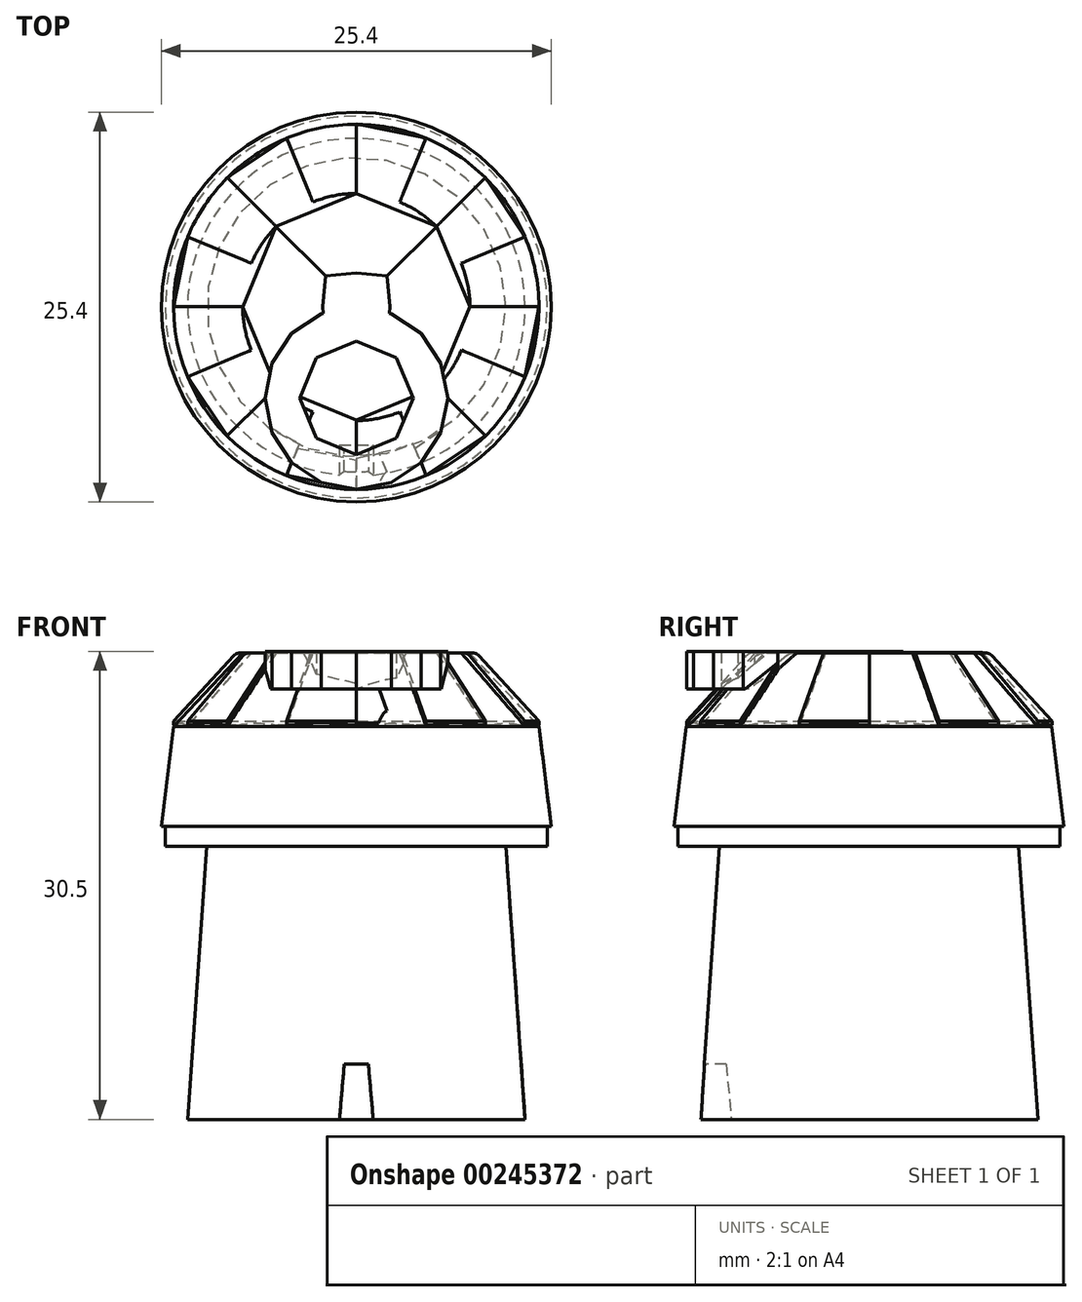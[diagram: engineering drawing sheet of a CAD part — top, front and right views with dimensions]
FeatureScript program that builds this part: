
annotation { "Feature Type Name" : "Feature", "Feature Type Description" : "" }
export const myFeature = defineFeature(function(context is Context, id is Id, definition is map)
    precondition{}
    {
        {
            var Q0;
            Q0=qCreatedBy(makeId("Front.planeOp"),FACE);
            var sketch = newSketch(context, id + "F0", { "sketchPlane" : qUnion([Q0])});
            skLineSegment(sketch, "E0", {"start": v(0, 0) * mm, "end": v(5.5, 0) * mm});
            skLineSegment(sketch, "E1", {"start": v(0, 8.9) * mm, "end": v(4.87, 8.9) * mm});
            skLineSegment(sketch, "E2", {"start": v(4.87, 8.9) * mm, "end": v(5.5, 0) * mm});
            skLineSegment(sketch, "E3", {"start": v(4.87, 8.9) * mm, "end": v(6.22, 8.9) * mm});
            skLineSegment(sketch, "E4", {"start": v(6.22, 8.9) * mm, "end": v(6.22, 9.55) * mm});
            skLineSegment(sketch, "E5", {"start": v(6.22, 9.55) * mm, "end": v(6.35, 9.55) * mm});
            skLineSegment(sketch, "E6", {"start": v(0, 0) * mm, "end": v(0, 15.2) * mm});
            skLineSegment(sketch, "E7", {"start": v(11.32, 12.8) * mm, "end": v(-3.84, 12.8) * mm, "construction": true});
            skLineSegment(sketch, "E8", {"start": v(5.95, 12.8) * mm, "end": v(6.35, 9.55) * mm});
            skLineSegment(sketch, "E9", {"start": v(15.11, 15.2) * mm, "end": v(0, 15.2) * mm, "construction": true});
            skLineSegment(sketch, "E10", {"start": v(0, 15.2) * mm, "end": v(3.7, 15.2) * mm});
            skLineSegment(sketch, "E11", {"start": v(3.7, 15.2) * mm, "end": v(5.95, 12.8) * mm});
            skSolve(sketch);
        }
        {
            var Q0;
            Q0=qSketchRegion(id+"F0",true);
            extrude(context, id + "F1", {"entities" : qUnion([Q0]), "depth" : 0.01 * mm});
        }
        {
            var Q0;
            Q0=makeQuery(id+"F1.opExtrude","CAP_FACE",FACE,{"disambiguationData":[OSD([sQuery(id+"F0.wireOp",EDGE,"E0"),sQuery(id+"F0.wireOp",EDGE,"E2"),sQuery(id+"F0.wireOp",EDGE,"E3"),sQuery(id+"F0.wireOp",EDGE,"E4"),sQuery(id+"F0.wireOp",EDGE,"E5"),sQuery(id+"F0.wireOp",EDGE,"sixM9Us5-RhuG-cWRY-0vQ0-8mJEDSYx7DVo"),sQuery(id+"F0.wireOp",EDGE,"EqexqkoD-ppkq-6j4X-MFRW-SI8jGCcGb6jM"),sQuery(id+"F0.wireOp",EDGE,"g6Ss7R6n-PE6a-QBEk-j47J-OcREIYiym4vq"),sQuery(id+"F0.wireOp",EDGE,"74306cc8-111f-4a76-b4a3-b401b2c3296c0.MirrorCS"),sQuery(id+"F0.wireOp",EDGE,"74306cc8-111f-4a76-b4a3-b401b2c3296c2.MirrorCS"),sQuery(id+"F0.wireOp",EDGE,"74306cc8-111f-4a76-b4a3-b401b2c3296c3.MirrorCS"),sQuery(id+"F0.wireOp",EDGE,"74306cc8-111f-4a76-b4a3-b401b2c3296c6.MirrorCS"),sQuery(id+"F0.wireOp",EDGE,"74306cc8-111f-4a76-b4a3-b401b2c3296c7.MirrorCS"),sQuery(id+"F0.wireOp",EDGE,"74306cc8-111f-4a76-b4a3-b401b2c3296c9.MirrorCS"),sQuery(id+"F0.wireOp",EDGE,"74306cc8-111f-4a76-b4a3-b401b2c3296c13.MirrorCS")])],"isStart":false});
            var Q1;
            Q1=makeQuery(id+"F1.opExtrude","CAP_EDGE",EDGE,{"disambiguationData":[OSD([sQuery(id+"F0.wireOp",EDGE,"E6")])],"isStart":false});
            revolve(context, id + "F2", {"operationType" : NewBodyOperationType.ADD, "entities" : qUnion([Q0]), "axis" : qUnion([Q1]), "revolveType" : RevolveType.FULL});
        }
        {
            var Q0;
            {var subQ0=sQuery(id+"F0.wireOp",EDGE,"E0");Q0=makeQuery(id+"F2.boolean.opBoolean","MERGE",FACE,{"derivedFrom":[makeQuery(id+"F1.opExtrude","SWEPT_FACE",FACE,{"disambiguationData":[OSD([subQ0])]}),makeQuery(id+"F2.opRevolve","SWEPT_FACE",FACE,{"disambiguationData":[OSD([subQ0])]})]});}
            var sketch = newSketch(context, id + "F3", { "sketchPlane" : qUnion([Q0])});
            skCircle(sketch, "E12", {"center": v(0, 0) * mm, "radius": 6 * mm, "construction": true});
            skLineSegment(sketch, "E13", {"start": v(0, 6) * mm, "end": v(0, 4.5) * mm, "construction": true});
            skLineSegment(sketch, "E14", {"start": v(0, 4.5) * mm, "end": v(0.55, 4.5) * mm});
            skLineSegment(sketch, "E15", {"start": v(0.55, 4.5) * mm, "end": v(0.55, 5.97) * mm});
            skLineSegment(sketch, "E16", {"start": v(0, 4.5) * mm, "end": v(-0.55, 4.5) * mm});
            skLineSegment(sketch, "E17", {"start": v(-0.55, 4.5) * mm, "end": v(-0.55, 5.97) * mm});
            skLineSegment(sketch, "E18", {"start": v(-0.55, 5.97) * mm, "end": v(0.55, 5.97) * mm});
            skSolve(sketch);
        }
        {
            var Q0;
            Q0=qSketchRegion(id+"F3",true);
            extrude(context, id + "F4", {"entities" : qUnion([Q0]), "operationType" : NewBodyOperationType.REMOVE, "oppositeDirection" : true, "depth" : 1.8 * mm});
        }
        {
            var Q0;
            Q0=makeQuery(id+"F4.boolean.opBoolean","COPY",EDGE,{"derivedFrom":makeQuery(id+"F4.opExtrude","CAP_EDGE",EDGE,{"disambiguationData":[OSD([sQuery(id+"F3.wireOp",EDGE,"E17")])],"isStart":false})});
            var Q1;
            Q1=makeQuery(id+"F4.boolean.opBoolean","COPY",EDGE,{"derivedFrom":makeQuery(id+"F4.opExtrude","CAP_EDGE",EDGE,{"disambiguationData":[OSD([sQuery(id+"F3.wireOp",EDGE,"E15")])],"isStart":false})});
            var Q2;
            Q2=makeQuery(id+"F4.boolean.opBoolean","COPY",EDGE,{"derivedFrom":makeQuery(id+"F4.opExtrude","CAP_EDGE",EDGE,{"disambiguationData":[OSD([sQuery(id+"F3.wireOp",EDGE,"E14"),sQuery(id+"F3.wireOp",EDGE,"E16")])],"isStart":false})});
            chamfer(context, id + "F5", {"entities" : qUnion([Q0, Q1, Q2]), "chamferType" : ChamferType.OFFSET_ANGLE, "width" : 1.8 * mm, "oppositeDirection" : false, "angle" : 5 * degree, "tangentPropagation" : true});
        }
        {
            var Q0;
            {var subQ0=sQuery(id+"F0.wireOp",EDGE,"E10");Q0=makeQuery(id+"F2.boolean.opBoolean","MERGE",FACE,{"derivedFrom":[makeQuery(id+"F1.opExtrude","SWEPT_FACE",FACE,{"disambiguationData":[OSD([subQ0])]}),makeQuery(id+"F2.opRevolve","SWEPT_FACE",FACE,{"disambiguationData":[OSD([subQ0])]})]});}
            var sketch = newSketch(context, id + "F6", { "sketchPlane" : qUnion([Q0])});
            skLineSegment(sketch, "E19.bottom", {"start": v(1, -1) * mm, "end": v(-1, -1) * mm, "construction": true});
            skLineSegment(sketch, "E19.top", {"start": v(1, 1) * mm, "end": v(-1, 1) * mm, "construction": true});
            skLineSegment(sketch, "E19.left", {"start": v(1, -1) * mm, "end": v(1, 1) * mm, "construction": true});
            skLineSegment(sketch, "E19.right", {"start": v(-1, -1) * mm, "end": v(-1, 1) * mm, "construction": true});
            skPoint(sketch, "E19.middle", {"position": v(0, 0) * mm});
            skLineSegment(sketch, "E20", {"start": v(0, 0) * mm, "end": v(1.1, 0) * mm, "construction": true});
            skPoint(sketch, "E20.endSnap0", {"position": v(1, 0) * mm});
            skLineSegment(sketch, "E21", {"start": v(0, 0) * mm, "end": v(0, 1.1) * mm, "construction": true});
            skPoint(sketch, "E21.endSnap0", {"position": v(0, 1) * mm});
            skLineSegment(sketch, "E22", {"start": v(0, 0) * mm, "end": v(-1.1, 0) * mm, "construction": true});
            skLineSegment(sketch, "E23", {"start": v(0, 0) * mm, "end": v(0, -1.1) * mm, "construction": true});
            skPoint(sketch, "E23.endSnap0", {"position": v(0, -1) * mm});
            skLineSegment(sketch, "E24", {"start": v(1, 1) * mm, "end": v(1.1, 0) * mm});
            skLineSegment(sketch, "E25", {"start": v(1, -1) * mm, "end": v(1.1, 0) * mm});
            skLineSegment(sketch, "E26", {"start": v(0, 1.1) * mm, "end": v(1, 1) * mm});
            skLineSegment(sketch, "E27", {"start": v(0, 1.1) * mm, "end": v(-1, 1) * mm});
            skLineSegment(sketch, "E28", {"start": v(-1, 1) * mm, "end": v(-1.1, 0) * mm});
            skLineSegment(sketch, "E29", {"start": v(-1, -1) * mm, "end": v(-1.1, 0) * mm});
            skLineSegment(sketch, "E30", {"start": v(-1, -1) * mm, "end": v(0, -1.1) * mm});
            skLineSegment(sketch, "E31", {"start": v(1, -1) * mm, "end": v(0, -1.1) * mm});
            skCircle(sketch, "E32", {"center": v(0, 0) * mm, "radius": 3.7 * mm, "construction": true});
            skLineSegment(sketch, "E33", {"start": v(0, -1.1) * mm, "end": v(0, -3.7) * mm, "construction": true});
            skLineSegment(sketch, "E34.bottom", {"start": v(2.62, -2.62) * mm, "end": v(-2.62, -2.62) * mm, "construction": true});
            skLineSegment(sketch, "E34.top", {"start": v(2.62, 2.62) * mm, "end": v(-2.62, 2.62) * mm, "construction": true});
            skLineSegment(sketch, "E34.left", {"start": v(2.62, -2.62) * mm, "end": v(2.62, 2.62) * mm, "construction": true});
            skLineSegment(sketch, "E34.right", {"start": v(-2.62, -2.62) * mm, "end": v(-2.62, 2.62) * mm, "construction": true});
            skLineSegment(sketch, "E35", {"start": v(-2.62, 2.62) * mm, "end": v(-1, 1) * mm});
            skLineSegment(sketch, "E36", {"start": v(-1, -1) * mm, "end": v(-2.62, -2.62) * mm});
            skLineSegment(sketch, "E37", {"start": v(1, -1) * mm, "end": v(2.62, -2.62) * mm});
            skLineSegment(sketch, "E38", {"start": v(1, 1) * mm, "end": v(2.62, 2.62) * mm});
            skLineSegment(sketch, "E39", {"start": v(-2.62, 2.62) * mm, "end": v(0, 3.69) * mm});
            skLineSegment(sketch, "E40", {"start": v(0, 3.69) * mm, "end": v(2.62, 2.62) * mm});
            skLineSegment(sketch, "E41", {"start": v(2.62, 2.62) * mm, "end": v(3.7, 0) * mm});
            skLineSegment(sketch, "E42", {"start": v(3.7, 0) * mm, "end": v(2.62, -2.62) * mm});
            skLineSegment(sketch, "E43", {"start": v(2.62, -2.62) * mm, "end": v(0, -3.7) * mm});
            skLineSegment(sketch, "E44", {"start": v(-2.62, -2.62) * mm, "end": v(0, -3.7) * mm});
            skLineSegment(sketch, "E45", {"start": v(-2.62, -2.62) * mm, "end": v(-3.7, 0) * mm});
            skLineSegment(sketch, "E46", {"start": v(-3.7, 0) * mm, "end": v(-2.62, 2.62) * mm});
            skSolve(sketch);
        }
        {
            var Q0;
            Q0=makeQuery(id+"F6.imprint","IMPRINT",FACE,{"disambiguationData":[TD([[makeQuery(id+"F6.imprint","IMPRINT",EDGE,{"derivedFrom":sQuery(id+"F6.wireOp",EDGE,"E24")}),-1.0]])]});
            extrude(context, id + "F7", {"entities" : qUnion([Q0]), "operationType" : NewBodyOperationType.ADD, "depth" : 0.05 * mm});
        }
        {
            var Q0;
            {var subQ1=sQuery(id+"F6.wireOp",EDGE,"E28");Q0=makeQuery(id+"F6.imprint","IMPRINT",FACE,{"disambiguationData":[TD([[makeQuery(id+"F6.imprint","IMPRINT",EDGE,{"derivedFrom":subQ1}),-1.0]])]});}
            var Q1;
            {var subQ1=sQuery(id+"F6.wireOp",EDGE,"E24");Q1=makeQuery(id+"F6.imprint","IMPRINT",FACE,{"disambiguationData":[TD([[makeQuery(id+"F6.imprint","IMPRINT",EDGE,{"derivedFrom":subQ1}),1.0]])]});}
            extrude(context, id + "F8", {"entities" : qUnion([Q0, Q1]), "operationType" : NewBodyOperationType.ADD, "depth" : 0.01 * mm});
        }
        {
            var Q0;
            Q0=makeQuery(id+"F6.imprint","IMPRINT",FACE,{"disambiguationData":[TD([[makeQuery(id+"F6.imprint","IMPRINT",EDGE,{"derivedFrom":sQuery(id+"F6.wireOp",EDGE,"E30")}),-1.0]])]});
            var Q1;
            {var subQ5=sQuery(id+"F6.wireOp",EDGE,"E26");Q1=makeQuery(id+"F6.imprint","IMPRINT",FACE,{"disambiguationData":[TD([[makeQuery(id+"F6.imprint","IMPRINT",EDGE,{"derivedFrom":subQ5}),1.0]])]});}
            extrude(context, id + "F9", {"entities" : qUnion([Q0, Q1]), "operationType" : NewBodyOperationType.ADD, "depth" : 0.02 * mm});
        }
        {
            var Q0;
            Q0=qCreatedBy(makeId("Top.planeOp"),FACE);
            cPlane(context, id + "F10", {"entities" : qUnion([Q0]), "cplaneType" : CPlaneType.OFFSET, "offset" : 15.2 * mm, "width" : 150 * mm, "height" : 150 * mm});
        }
        {
            var Q0;
            Q0=qCreatedBy(id+"F10.planeOp",FACE);
            var sketch = newSketch(context, id + "F11", { "sketchPlane" : qUnion([Q0])});
            skLineSegment(sketch, "E47", {"start": v(0, -5.95) * mm, "end": v(0, -3.7) * mm});
            skLineSegment(sketch, "E48", {"start": v(1.3, -3.16) * mm, "end": v(2.28, -5.5) * mm});
            skLineSegment(sketch, "E49.1.0", {"start": v(4.2, -4.2) * mm, "end": v(2.62, -2.62) * mm});
            skLineSegment(sketch, "E49.1.1", {"start": v(3.16, -1.3) * mm, "end": v(5.5, -2.28) * mm});
            skLineSegment(sketch, "E49.2.0", {"start": v(5.95, 0) * mm, "end": v(3.7, 0) * mm});
            skLineSegment(sketch, "E49.2.1", {"start": v(3.16, 1.3) * mm, "end": v(5.5, 2.28) * mm});
            skPoint(sketch, "E49.center", {"position": v(0, 0) * mm});
            skLineSegment(sketch, "E50.1.3.0", {"start": v(4.2, 4.2) * mm, "end": v(2.62, 2.62) * mm});
            skLineSegment(sketch, "E50.3.3.0", {"start": v(1.3, 3.16) * mm, "end": v(2.28, 5.5) * mm});
            skLineSegment(sketch, "E50.1.4.0", {"start": v(0, 5.95) * mm, "end": v(0, 3.7) * mm});
            skLineSegment(sketch, "E50.3.4.0", {"start": v(-1.3, 3.16) * mm, "end": v(-2.28, 5.5) * mm});
            skLineSegment(sketch, "E50.1.5.0", {"start": v(-4.2, 4.2) * mm, "end": v(-2.62, 2.62) * mm});
            skLineSegment(sketch, "E50.3.5.0", {"start": v(-3.16, 1.3) * mm, "end": v(-5.5, 2.28) * mm});
            skLineSegment(sketch, "E50.1.6.0", {"start": v(-5.95, 0) * mm, "end": v(-3.7, 0) * mm});
            skLineSegment(sketch, "E50.3.6.0", {"start": v(-3.16, -1.3) * mm, "end": v(-5.5, -2.28) * mm});
            skLineSegment(sketch, "E50.1.7.0", {"start": v(-4.2, -4.2) * mm, "end": v(-2.62, -2.62) * mm});
            skLineSegment(sketch, "E50.3.7.0", {"start": v(-1.3, -3.16) * mm, "end": v(-2.28, -5.5) * mm});
            skLineSegment(sketch, "E51", {"start": v(0, -3.7) * mm, "end": v(1.3, -3.16) * mm});
            skLineSegment(sketch, "E52", {"start": v(1.3, -3.16) * mm, "end": v(2.62, -2.62) * mm});
            skLineSegment(sketch, "E53", {"start": v(2.62, -2.62) * mm, "end": v(3.16, -1.3) * mm});
            skLineSegment(sketch, "E54", {"start": v(3.16, -1.3) * mm, "end": v(3.7, 0) * mm});
            skLineSegment(sketch, "E55", {"start": v(3.7, 0) * mm, "end": v(3.16, 1.3) * mm});
            skLineSegment(sketch, "E56", {"start": v(3.16, 1.3) * mm, "end": v(2.62, 2.62) * mm});
            skLineSegment(sketch, "E57", {"start": v(2.62, 2.62) * mm, "end": v(1.3, 3.16) * mm});
            skLineSegment(sketch, "E58", {"start": v(1.3, 3.16) * mm, "end": v(0, 3.7) * mm});
            skLineSegment(sketch, "E59", {"start": v(0, 3.7) * mm, "end": v(-1.3, 3.16) * mm});
            skLineSegment(sketch, "E60", {"start": v(-1.3, 3.16) * mm, "end": v(-2.62, 2.62) * mm});
            skLineSegment(sketch, "E61", {"start": v(-2.62, 2.62) * mm, "end": v(-3.16, 1.3) * mm});
            skLineSegment(sketch, "E62", {"start": v(-3.16, 1.3) * mm, "end": v(-3.7, 0) * mm});
            skLineSegment(sketch, "E63", {"start": v(-3.7, 0) * mm, "end": v(-3.16, -1.3) * mm});
            skLineSegment(sketch, "E64", {"start": v(-3.16, -1.3) * mm, "end": v(-2.62, -2.62) * mm});
            skLineSegment(sketch, "E65", {"start": v(-2.62, -2.62) * mm, "end": v(-1.3, -3.16) * mm});
            skLineSegment(sketch, "E66", {"start": v(-1.3, -3.16) * mm, "end": v(0, -3.7) * mm});
            skLineSegment(sketch, "E67", {"start": v(-2.28, -5.5) * mm, "end": v(0, -5.95) * mm});
            skLineSegment(sketch, "E68", {"start": v(0, -5.95) * mm, "end": v(2.28, -5.5) * mm});
            skLineSegment(sketch, "E69", {"start": v(2.28, -5.5) * mm, "end": v(4.2, -4.2) * mm});
            skLineSegment(sketch, "E70", {"start": v(4.2, -4.2) * mm, "end": v(5.5, -2.28) * mm});
            skLineSegment(sketch, "E71", {"start": v(5.5, -2.28) * mm, "end": v(5.95, 0) * mm});
            skLineSegment(sketch, "E72", {"start": v(5.95, 0) * mm, "end": v(5.5, 2.28) * mm});
            skLineSegment(sketch, "E73", {"start": v(5.5, 2.28) * mm, "end": v(4.2, 4.2) * mm});
            skLineSegment(sketch, "E74", {"start": v(4.2, 4.2) * mm, "end": v(2.28, 5.5) * mm});
            skLineSegment(sketch, "E75", {"start": v(2.28, 5.5) * mm, "end": v(0, 5.95) * mm});
            skLineSegment(sketch, "E76", {"start": v(0, 5.95) * mm, "end": v(-2.28, 5.5) * mm});
            skLineSegment(sketch, "E77", {"start": v(-2.28, 5.5) * mm, "end": v(-4.2, 4.2) * mm});
            skLineSegment(sketch, "E78", {"start": v(-4.2, 4.2) * mm, "end": v(-5.5, 2.28) * mm});
            skLineSegment(sketch, "E79", {"start": v(-5.5, 2.28) * mm, "end": v(-5.95, 0) * mm});
            skLineSegment(sketch, "E80", {"start": v(-5.95, 0) * mm, "end": v(-5.5, -2.28) * mm});
            skLineSegment(sketch, "E81", {"start": v(-5.5, -2.28) * mm, "end": v(-4.2, -4.2) * mm});
            skLineSegment(sketch, "E82", {"start": v(-4.2, -4.2) * mm, "end": v(-2.28, -5.5) * mm});
            skSolve(sketch);
        }
        {
            var Q0;
            Q0=makeQuery(id+"F11.imprint","IMPRINT",FACE,{"disambiguationData":[TD([[makeQuery(id+"F11.imprint","IMPRINT",EDGE,{"derivedFrom":sQuery(id+"F11.wireOp",EDGE,"E47")}),1.0]])]});
            var Q1;
            Q1=makeQuery(id+"F11.imprint","IMPRINT",FACE,{"disambiguationData":[TD([[makeQuery(id+"F11.imprint","IMPRINT",EDGE,{"derivedFrom":sQuery(id+"F11.wireOp",EDGE,"E48")}),1.0]])]});
            var Q2;
            Q2=makeQuery(id+"F11.imprint","IMPRINT",FACE,{"disambiguationData":[TD([[makeQuery(id+"F11.imprint","IMPRINT",EDGE,{"derivedFrom":sQuery(id+"F11.wireOp",EDGE,"E49.1.1")}),1.0]])]});
            var Q3;
            Q3=makeQuery(id+"F11.imprint","IMPRINT",FACE,{"disambiguationData":[TD([[makeQuery(id+"F11.imprint","IMPRINT",EDGE,{"derivedFrom":sQuery(id+"F11.wireOp",EDGE,"E49.2.1")}),1.0]])]});
            var Q4;
            Q4=makeQuery(id+"F11.imprint","IMPRINT",FACE,{"disambiguationData":[TD([[makeQuery(id+"F11.imprint","IMPRINT",EDGE,{"derivedFrom":sQuery(id+"F11.wireOp",EDGE,"E50.3.3.0")}),1.0]])]});
            var Q5;
            Q5=makeQuery(id+"F11.imprint","IMPRINT",FACE,{"disambiguationData":[TD([[makeQuery(id+"F11.imprint","IMPRINT",EDGE,{"derivedFrom":sQuery(id+"F11.wireOp",EDGE,"E50.3.4.0")}),1.0]])]});
            var Q6;
            Q6=makeQuery(id+"F11.imprint","IMPRINT",FACE,{"disambiguationData":[TD([[makeQuery(id+"F11.imprint","IMPRINT",EDGE,{"derivedFrom":sQuery(id+"F11.wireOp",EDGE,"E50.3.5.0")}),1.0]])]});
            var Q7;
            Q7=makeQuery(id+"F11.imprint","IMPRINT",FACE,{"disambiguationData":[TD([[makeQuery(id+"F11.imprint","IMPRINT",EDGE,{"derivedFrom":sQuery(id+"F11.wireOp",EDGE,"E50.3.6.0")}),1.0]])]});
            var Q8;
            Q8=makeQuery(id+"F1.opExtrude","SWEPT_BODY",BODY,{"disambiguationData":[OSD([sQuery(id+"F0.wireOp",EDGE,"E0"),sQuery(id+"F0.wireOp",EDGE,"E2"),sQuery(id+"F0.wireOp",EDGE,"E3"),sQuery(id+"F0.wireOp",EDGE,"E4"),sQuery(id+"F0.wireOp",EDGE,"E5"),sQuery(id+"F0.wireOp",EDGE,"E6"),sQuery(id+"F0.wireOp",EDGE,"E8"),sQuery(id+"F0.wireOp",EDGE,"E10"),sQuery(id+"F0.wireOp",EDGE,"E11")])]});
            extrude(context, id + "F12", {"entities" : qUnion([Q0, Q1, Q2, Q3, Q4, Q5, Q6, Q7]), "operationType" : NewBodyOperationType.ADD, "oppositeDirection" : true, "endBoundEntityBody" : qUnion([Q8]), "depth" : 2.35 * mm});
        }
        {
            var Q0;
            Q0=makeQuery(id+"F12.opExtrude","CAP_EDGE",EDGE,{"disambiguationData":[OSD([sQuery(id+"F11.wireOp",EDGE,"E67")])],"isStart":true});
            var Q1;
            Q1=makeQuery(id+"F12.opExtrude","CAP_EDGE",EDGE,{"disambiguationData":[OSD([sQuery(id+"F11.wireOp",EDGE,"E69")])],"isStart":true});
            var Q2;
            Q2=makeQuery(id+"F12.opExtrude","CAP_EDGE",EDGE,{"disambiguationData":[OSD([sQuery(id+"F11.wireOp",EDGE,"E71")])],"isStart":true});
            var Q3;
            Q3=makeQuery(id+"F12.opExtrude","CAP_EDGE",EDGE,{"disambiguationData":[OSD([sQuery(id+"F11.wireOp",EDGE,"E73")])],"isStart":true});
            var Q4;
            Q4=makeQuery(id+"F12.opExtrude","CAP_EDGE",EDGE,{"disambiguationData":[OSD([sQuery(id+"F11.wireOp",EDGE,"E75")])],"isStart":true});
            var Q5;
            Q5=makeQuery(id+"F12.opExtrude","CAP_EDGE",EDGE,{"disambiguationData":[OSD([sQuery(id+"F11.wireOp",EDGE,"E77")])],"isStart":true});
            var Q6;
            Q6=makeQuery(id+"F12.opExtrude","CAP_EDGE",EDGE,{"disambiguationData":[OSD([sQuery(id+"F11.wireOp",EDGE,"E79")])],"isStart":true});
            var Q7;
            Q7=makeQuery(id+"F12.opExtrude","CAP_EDGE",EDGE,{"disambiguationData":[OSD([sQuery(id+"F11.wireOp",EDGE,"E81")])],"isStart":true});
            chamfer(context, id + "F13", {"entities" : qUnion([Q0, Q1, Q2, Q3, Q4, Q5, Q6, Q7]), "chamferType" : ChamferType.OFFSET_ANGLE, "width" : 2 * mm, "oppositeDirection" : false, "angle" : 48 * degree, "tangentPropagation" : true});
        }
        {
            var Q0;
            Q0=makeQuery(id+"F11.imprint","IMPRINT",FACE,{"disambiguationData":[TD([[makeQuery(id+"F11.imprint","IMPRINT",EDGE,{"derivedFrom":sQuery(id+"F11.wireOp",EDGE,"E47")}),-1.0]])]});
            var Q1;
            Q1=makeQuery(id+"F11.imprint","IMPRINT",FACE,{"disambiguationData":[TD([[makeQuery(id+"F11.imprint","IMPRINT",EDGE,{"derivedFrom":sQuery(id+"F11.wireOp",EDGE,"E49.1.0")}),-1.0]])]});
            var Q2;
            Q2=makeQuery(id+"F11.imprint","IMPRINT",FACE,{"disambiguationData":[TD([[makeQuery(id+"F11.imprint","IMPRINT",EDGE,{"derivedFrom":sQuery(id+"F11.wireOp",EDGE,"E49.2.0")}),-1.0]])]});
            var Q3;
            Q3=makeQuery(id+"F11.imprint","IMPRINT",FACE,{"disambiguationData":[TD([[makeQuery(id+"F11.imprint","IMPRINT",EDGE,{"derivedFrom":sQuery(id+"F11.wireOp",EDGE,"E50.1.3.0")}),-1.0]])]});
            var Q4;
            Q4=makeQuery(id+"F11.imprint","IMPRINT",FACE,{"disambiguationData":[TD([[makeQuery(id+"F11.imprint","IMPRINT",EDGE,{"derivedFrom":sQuery(id+"F11.wireOp",EDGE,"E50.1.4.0")}),-1.0]])]});
            var Q5;
            Q5=makeQuery(id+"F11.imprint","IMPRINT",FACE,{"disambiguationData":[TD([[makeQuery(id+"F11.imprint","IMPRINT",EDGE,{"derivedFrom":sQuery(id+"F11.wireOp",EDGE,"E50.1.5.0")}),-1.0]])]});
            var Q6;
            Q6=makeQuery(id+"F11.imprint","IMPRINT",FACE,{"disambiguationData":[TD([[makeQuery(id+"F11.imprint","IMPRINT",EDGE,{"derivedFrom":sQuery(id+"F11.wireOp",EDGE,"E50.1.6.0")}),-1.0]])]});
            var Q7;
            Q7=makeQuery(id+"F11.imprint","IMPRINT",FACE,{"disambiguationData":[TD([[makeQuery(id+"F11.imprint","IMPRINT",EDGE,{"derivedFrom":sQuery(id+"F11.wireOp",EDGE,"E50.1.7.0")}),-1.0]])]});
            extrude(context, id + "F14", {"entities" : qUnion([Q0, Q1, Q2, Q3, Q4, Q5, Q6, Q7]), "oppositeDirection" : true, "depth" : 2.45 * mm});
        }
        {
            var Q0;
            Q0=makeQuery(id+"F14.opExtrude","CAP_EDGE",EDGE,{"disambiguationData":[OSD([sQuery(id+"F11.wireOp",EDGE,"E82")])],"isStart":true});
            var Q1;
            Q1=makeQuery(id+"F14.opExtrude","CAP_EDGE",EDGE,{"disambiguationData":[OSD([sQuery(id+"F11.wireOp",EDGE,"E68")])],"isStart":true});
            var Q2;
            Q2=makeQuery(id+"F14.opExtrude","CAP_EDGE",EDGE,{"disambiguationData":[OSD([sQuery(id+"F11.wireOp",EDGE,"E70")])],"isStart":true});
            var Q3;
            Q3=makeQuery(id+"F14.opExtrude","CAP_EDGE",EDGE,{"disambiguationData":[OSD([sQuery(id+"F11.wireOp",EDGE,"E72")])],"isStart":true});
            var Q4;
            Q4=makeQuery(id+"F14.opExtrude","CAP_EDGE",EDGE,{"disambiguationData":[OSD([sQuery(id+"F11.wireOp",EDGE,"E74")])],"isStart":true});
            var Q5;
            Q5=makeQuery(id+"F14.opExtrude","CAP_EDGE",EDGE,{"disambiguationData":[OSD([sQuery(id+"F11.wireOp",EDGE,"E76")])],"isStart":true});
            var Q6;
            Q6=makeQuery(id+"F14.opExtrude","CAP_EDGE",EDGE,{"disambiguationData":[OSD([sQuery(id+"F11.wireOp",EDGE,"E78")])],"isStart":true});
            var Q7;
            Q7=makeQuery(id+"F14.opExtrude","CAP_EDGE",EDGE,{"disambiguationData":[OSD([sQuery(id+"F11.wireOp",EDGE,"E80")])],"isStart":true});
            chamfer(context, id + "F15", {"entities" : qUnion([Q0, Q1, Q2, Q3, Q4, Q5, Q6, Q7]), "chamferType" : ChamferType.OFFSET_ANGLE, "width" : 2 * mm, "oppositeDirection" : false, "angle" : 48 * degree, "tangentPropagation" : true});
        }
        {
            var Q0;
            Q0=makeQuery(id+"F1.opExtrude","SWEPT_BODY",BODY,{"disambiguationData":[OSD([sQuery(id+"F0.wireOp",EDGE,"E0"),sQuery(id+"F0.wireOp",EDGE,"E2"),sQuery(id+"F0.wireOp",EDGE,"E3"),sQuery(id+"F0.wireOp",EDGE,"E4"),sQuery(id+"F0.wireOp",EDGE,"E5"),sQuery(id+"F0.wireOp",EDGE,"E6"),sQuery(id+"F0.wireOp",EDGE,"E8"),sQuery(id+"F0.wireOp",EDGE,"E10"),sQuery(id+"F0.wireOp",EDGE,"E11")])]});
            var Q1;
            Q1=makeQuery(id+"F12.opExtrude","CAP_VERTEX",VERTEX,{"disambiguationData":[OSD([sQuery(id+"F11.wireOp",EDGE,"E47"),sQuery(id+"F11.wireOp",EDGE,"E67"),sQuery(id+"F11.wireOp",EDGE,"E68")])],"isStart":false});
            transform(context, id + "F16", {"entities" : qUnion([Q0]), "transformType" : TransformType.SCALE_UNIFORMLY, "scale" : 2, "scalePoint" : qUnion([Q1]), "makeCopy" : false});
        }
        {
            var Q0;
            {var subQ0=sQuery(id+"F11.wireOp",EDGE,"E79");var subQ1=sQuery(id+"F0.wireOp",EDGE,"E10");var subQ2=makeQuery(id+"F1.opExtrude","SWEPT_FACE",FACE,{"disambiguationData":[OSD([subQ1])]});var subQ3=sQuery(id+"F0.wireOp",EDGE,"E11");var subQ4=makeQuery(id+"F2.opRevolve","SWEPT_FACE",FACE,{"disambiguationData":[OSD([subQ1])]});var subQ5=sQuery(id+"F6.wireOp",EDGE,"E46");var subQ6=makeQuery(id+"F2.opRevolve","SWEPT_EDGE",EDGE,{"disambiguationData":[OSD([subQ1,subQ3])]});Q0=makeQuery(id+"F13.opChamfer","BLEND_EDGE",EDGE,{"blendedFrom":[makeQuery(id+"F12.opExtrude","CAP_EDGE",EDGE,{"disambiguationData":[OSD([subQ0])],"isStart":true}),makeQuery(id+"F12.boolean.opBoolean","MERGE",FACE,{"derivedFrom":[makeQuery(id+"F8.boolean.opBoolean","SPLIT",FACE,{"disambiguationData":[TD([subQ2,subQ4,makeQuery(id+"F2.opRevolve","SWEPT_FACE",FACE,{"disambiguationData":[OSD([subQ3])]}),makeQuery(id+"F8.opExtrude","SWEPT_FACE",FACE,{"disambiguationData":[OSD([sQuery(id+"F6.wireOp",EDGE,"E45")])]}),makeQuery(id+"F8.opExtrude","SWEPT_FACE",FACE,{"disambiguationData":[OSD([subQ5])]}),makeQuery(id+"F8.opExtrude","SWEPT_FACE",FACE,{"disambiguationData":[OSD([subQ1,subQ3]),TDD([makeQuery(id+"F6.imprint","IMPRINT",EDGE,{"disambiguationData":[TD([[makeQuery(id+"F6.imprint","INTERSECT",VERTEX,{"derivedFrom":[subQ6,subQ5]}),1.0]])],"derivedFrom":subQ6})])]})])],"derivedFrom":makeQuery(id+"F2.boolean.opBoolean","MERGE",FACE,{"derivedFrom":[subQ2,subQ4]})}),makeQuery(id+"F12.opExtrude","CAP_FACE",FACE,{"disambiguationData":[OSD([sQuery(id+"F11.wireOp",EDGE,"E50.3.5.0"),sQuery(id+"F11.wireOp",EDGE,"E50.1.6.0"),sQuery(id+"F11.wireOp",EDGE,"E62"),subQ0])],"isStart":true})]})],"blendedInto":[makeQuery(id+"F12.boolean.opBoolean","MERGE",FACE,{"derivedFrom":[makeQuery(id+"F8.boolean.opBoolean","SPLIT",FACE,{"disambiguationData":[TD([subQ2,subQ4,makeQuery(id+"F2.opRevolve","SWEPT_FACE",FACE,{"disambiguationData":[OSD([subQ3])]}),makeQuery(id+"F8.opExtrude","SWEPT_FACE",FACE,{"disambiguationData":[OSD([sQuery(id+"F6.wireOp",EDGE,"E45")])]}),makeQuery(id+"F8.opExtrude","SWEPT_FACE",FACE,{"disambiguationData":[OSD([subQ5])]}),makeQuery(id+"F8.opExtrude","SWEPT_FACE",FACE,{"disambiguationData":[OSD([subQ1,subQ3]),TDD([makeQuery(id+"F6.imprint","IMPRINT",EDGE,{"disambiguationData":[TD([[makeQuery(id+"F6.imprint","INTERSECT",VERTEX,{"derivedFrom":[subQ6,subQ5]}),1.0]])],"derivedFrom":subQ6})])]})])],"derivedFrom":makeQuery(id+"F2.boolean.opBoolean","MERGE",FACE,{"derivedFrom":[subQ2,subQ4]})}),makeQuery(id+"F12.opExtrude","CAP_FACE",FACE,{"disambiguationData":[OSD([sQuery(id+"F11.wireOp",EDGE,"E50.3.5.0"),sQuery(id+"F11.wireOp",EDGE,"E50.1.6.0"),sQuery(id+"F11.wireOp",EDGE,"E62"),subQ0])],"isStart":true})]})]});}
            var Q1;
            {var subQ0=sQuery(id+"F11.wireOp",EDGE,"E77");var subQ1=sQuery(id+"F6.wireOp",EDGE,"E39");var subQ2=sQuery(id+"F0.wireOp",EDGE,"E11");var subQ3=makeQuery(id+"F2.opRevolve","SWEPT_FACE",FACE,{"disambiguationData":[OSD([subQ2])]});var subQ4=sQuery(id+"F0.wireOp",EDGE,"E10");var subQ5=makeQuery(id+"F2.opRevolve","SWEPT_FACE",FACE,{"disambiguationData":[OSD([subQ4])]});var subQ6=makeQuery(id+"F1.opExtrude","SWEPT_FACE",FACE,{"disambiguationData":[OSD([subQ4])]});var subQ7=makeQuery(id+"F2.opRevolve","SWEPT_EDGE",EDGE,{"disambiguationData":[OSD([subQ4,subQ2])]});var subQ8=sQuery(id+"F6.wireOp",EDGE,"E35");var subQ10=sQuery(id+"F6.wireOp",EDGE,"E38");Q1=makeQuery(id+"F13.opChamfer","BLEND_EDGE",EDGE,{"blendedFrom":[makeQuery(id+"F12.opExtrude","CAP_EDGE",EDGE,{"disambiguationData":[OSD([subQ0])],"isStart":true}),makeQuery(id+"F12.boolean.opBoolean","MERGE",FACE,{"derivedFrom":[makeQuery(id+"F9.boolean.opBoolean","SPLIT",FACE,{"disambiguationData":[TD([makeQuery(id+"F9.opExtrude","SWEPT_FACE",FACE,{"disambiguationData":[OSD([subQ4,subQ2]),TDD([makeQuery(id+"F6.imprint","IMPRINT",EDGE,{"disambiguationData":[TD([[makeQuery(id+"F6.imprint","INTERSECT",VERTEX,{"derivedFrom":[subQ7,subQ1]}),-1.0]])],"derivedFrom":subQ7})])]})])],"derivedFrom":makeQuery(id+"F8.boolean.opBoolean","SPLIT",FACE,{"disambiguationData":[TD([subQ3,makeQuery(id+"F7.opExtrude","SWEPT_FACE",FACE,{"disambiguationData":[OSD([sQuery(id+"F6.wireOp",EDGE,"E26")])]}),makeQuery(id+"F7.opExtrude","SWEPT_FACE",FACE,{"disambiguationData":[OSD([sQuery(id+"F6.wireOp",EDGE,"E27")])]}),makeQuery(id+"F8.opExtrude","SWEPT_FACE",FACE,{"disambiguationData":[OSD([subQ8])]}),makeQuery(id+"F8.opExtrude","SWEPT_FACE",FACE,{"disambiguationData":[OSD([subQ10])]}),makeQuery(id+"F8.opExtrude","SWEPT_FACE",FACE,{"disambiguationData":[OSD([subQ4,subQ2]),TDD([makeQuery(id+"F6.imprint","IMPRINT",EDGE,{"disambiguationData":[TD([[makeQuery(id+"F6.imprint","INTERSECT",VERTEX,{"derivedFrom":[subQ7,sQuery(id+"F6.wireOp",EDGE,"E41")]}),-1.0]])],"derivedFrom":subQ7})])]}),makeQuery(id+"F8.opExtrude","SWEPT_FACE",FACE,{"disambiguationData":[OSD([subQ4,subQ2]),TDD([makeQuery(id+"F6.imprint","IMPRINT",EDGE,{"disambiguationData":[TD([[makeQuery(id+"F6.imprint","INTERSECT",VERTEX,{"derivedFrom":[subQ7,sQuery(id+"F6.wireOp",EDGE,"E46")]}),1.0]])],"derivedFrom":subQ7})])]})])],"derivedFrom":makeQuery(id+"F2.boolean.opBoolean","MERGE",FACE,{"derivedFrom":[subQ6,subQ5]})})}),makeQuery(id+"F12.opExtrude","CAP_FACE",FACE,{"disambiguationData":[OSD([sQuery(id+"F11.wireOp",EDGE,"E50.3.4.0"),sQuery(id+"F11.wireOp",EDGE,"E50.1.5.0"),sQuery(id+"F11.wireOp",EDGE,"E60"),subQ0])],"isStart":true})]})],"blendedInto":[makeQuery(id+"F12.boolean.opBoolean","MERGE",FACE,{"derivedFrom":[makeQuery(id+"F9.boolean.opBoolean","SPLIT",FACE,{"disambiguationData":[TD([makeQuery(id+"F9.opExtrude","SWEPT_FACE",FACE,{"disambiguationData":[OSD([subQ4,subQ2]),TDD([makeQuery(id+"F6.imprint","IMPRINT",EDGE,{"disambiguationData":[TD([[makeQuery(id+"F6.imprint","INTERSECT",VERTEX,{"derivedFrom":[subQ7,subQ1]}),-1.0]])],"derivedFrom":subQ7})])]})])],"derivedFrom":makeQuery(id+"F8.boolean.opBoolean","SPLIT",FACE,{"disambiguationData":[TD([subQ3,makeQuery(id+"F7.opExtrude","SWEPT_FACE",FACE,{"disambiguationData":[OSD([sQuery(id+"F6.wireOp",EDGE,"E26")])]}),makeQuery(id+"F7.opExtrude","SWEPT_FACE",FACE,{"disambiguationData":[OSD([sQuery(id+"F6.wireOp",EDGE,"E27")])]}),makeQuery(id+"F8.opExtrude","SWEPT_FACE",FACE,{"disambiguationData":[OSD([subQ8])]}),makeQuery(id+"F8.opExtrude","SWEPT_FACE",FACE,{"disambiguationData":[OSD([subQ10])]}),makeQuery(id+"F8.opExtrude","SWEPT_FACE",FACE,{"disambiguationData":[OSD([subQ4,subQ2]),TDD([makeQuery(id+"F6.imprint","IMPRINT",EDGE,{"disambiguationData":[TD([[makeQuery(id+"F6.imprint","INTERSECT",VERTEX,{"derivedFrom":[subQ7,sQuery(id+"F6.wireOp",EDGE,"E41")]}),-1.0]])],"derivedFrom":subQ7})])]}),makeQuery(id+"F8.opExtrude","SWEPT_FACE",FACE,{"disambiguationData":[OSD([subQ4,subQ2]),TDD([makeQuery(id+"F6.imprint","IMPRINT",EDGE,{"disambiguationData":[TD([[makeQuery(id+"F6.imprint","INTERSECT",VERTEX,{"derivedFrom":[subQ7,sQuery(id+"F6.wireOp",EDGE,"E46")]}),1.0]])],"derivedFrom":subQ7})])]})])],"derivedFrom":makeQuery(id+"F2.boolean.opBoolean","MERGE",FACE,{"derivedFrom":[subQ6,subQ5]})})}),makeQuery(id+"F12.opExtrude","CAP_FACE",FACE,{"disambiguationData":[OSD([sQuery(id+"F11.wireOp",EDGE,"E50.3.4.0"),sQuery(id+"F11.wireOp",EDGE,"E50.1.5.0"),sQuery(id+"F11.wireOp",EDGE,"E60"),subQ0])],"isStart":true})]})]});}
            var Q2;
            {var subQ0=sQuery(id+"F11.wireOp",EDGE,"E75");var subQ1=sQuery(id+"F0.wireOp",EDGE,"E11");var subQ2=makeQuery(id+"F2.opRevolve","SWEPT_FACE",FACE,{"disambiguationData":[OSD([subQ1])]});var subQ3=sQuery(id+"F0.wireOp",EDGE,"E10");var subQ4=makeQuery(id+"F2.opRevolve","SWEPT_FACE",FACE,{"disambiguationData":[OSD([subQ3])]});var subQ5=makeQuery(id+"F1.opExtrude","SWEPT_FACE",FACE,{"disambiguationData":[OSD([subQ3])]});var subQ6=sQuery(id+"F6.wireOp",EDGE,"E40");var subQ7=makeQuery(id+"F2.opRevolve","SWEPT_EDGE",EDGE,{"disambiguationData":[OSD([subQ3,subQ1])]});var subQ8=sQuery(id+"F6.wireOp",EDGE,"E38");var subQ10=sQuery(id+"F6.wireOp",EDGE,"E35");Q2=makeQuery(id+"F13.opChamfer","BLEND_EDGE",EDGE,{"blendedFrom":[makeQuery(id+"F12.opExtrude","CAP_EDGE",EDGE,{"disambiguationData":[OSD([subQ0])],"isStart":true}),makeQuery(id+"F12.boolean.opBoolean","MERGE",FACE,{"derivedFrom":[makeQuery(id+"F9.boolean.opBoolean","SPLIT",FACE,{"disambiguationData":[TD([makeQuery(id+"F9.opExtrude","SWEPT_FACE",FACE,{"disambiguationData":[OSD([subQ3,subQ1]),TDD([makeQuery(id+"F6.imprint","IMPRINT",EDGE,{"disambiguationData":[TD([[makeQuery(id+"F6.imprint","INTERSECT",VERTEX,{"derivedFrom":[subQ7,subQ6]}),1.0]])],"derivedFrom":subQ7})])]})])],"derivedFrom":makeQuery(id+"F8.boolean.opBoolean","SPLIT",FACE,{"disambiguationData":[TD([subQ2,makeQuery(id+"F7.opExtrude","SWEPT_FACE",FACE,{"disambiguationData":[OSD([sQuery(id+"F6.wireOp",EDGE,"E26")])]}),makeQuery(id+"F7.opExtrude","SWEPT_FACE",FACE,{"disambiguationData":[OSD([sQuery(id+"F6.wireOp",EDGE,"E27")])]}),makeQuery(id+"F8.opExtrude","SWEPT_FACE",FACE,{"disambiguationData":[OSD([subQ10])]}),makeQuery(id+"F8.opExtrude","SWEPT_FACE",FACE,{"disambiguationData":[OSD([subQ8])]}),makeQuery(id+"F8.opExtrude","SWEPT_FACE",FACE,{"disambiguationData":[OSD([subQ3,subQ1]),TDD([makeQuery(id+"F6.imprint","IMPRINT",EDGE,{"disambiguationData":[TD([[makeQuery(id+"F6.imprint","INTERSECT",VERTEX,{"derivedFrom":[subQ7,sQuery(id+"F6.wireOp",EDGE,"E41")]}),-1.0]])],"derivedFrom":subQ7})])]}),makeQuery(id+"F8.opExtrude","SWEPT_FACE",FACE,{"disambiguationData":[OSD([subQ3,subQ1]),TDD([makeQuery(id+"F6.imprint","IMPRINT",EDGE,{"disambiguationData":[TD([[makeQuery(id+"F6.imprint","INTERSECT",VERTEX,{"derivedFrom":[subQ7,sQuery(id+"F6.wireOp",EDGE,"E46")]}),1.0]])],"derivedFrom":subQ7})])]})])],"derivedFrom":makeQuery(id+"F2.boolean.opBoolean","MERGE",FACE,{"derivedFrom":[subQ5,subQ4]})})}),makeQuery(id+"F12.opExtrude","CAP_FACE",FACE,{"disambiguationData":[OSD([sQuery(id+"F11.wireOp",EDGE,"E50.3.3.0"),sQuery(id+"F11.wireOp",EDGE,"E50.1.4.0"),sQuery(id+"F11.wireOp",EDGE,"E58"),subQ0])],"isStart":true})]})],"blendedInto":[makeQuery(id+"F12.boolean.opBoolean","MERGE",FACE,{"derivedFrom":[makeQuery(id+"F9.boolean.opBoolean","SPLIT",FACE,{"disambiguationData":[TD([makeQuery(id+"F9.opExtrude","SWEPT_FACE",FACE,{"disambiguationData":[OSD([subQ3,subQ1]),TDD([makeQuery(id+"F6.imprint","IMPRINT",EDGE,{"disambiguationData":[TD([[makeQuery(id+"F6.imprint","INTERSECT",VERTEX,{"derivedFrom":[subQ7,subQ6]}),1.0]])],"derivedFrom":subQ7})])]})])],"derivedFrom":makeQuery(id+"F8.boolean.opBoolean","SPLIT",FACE,{"disambiguationData":[TD([subQ2,makeQuery(id+"F7.opExtrude","SWEPT_FACE",FACE,{"disambiguationData":[OSD([sQuery(id+"F6.wireOp",EDGE,"E26")])]}),makeQuery(id+"F7.opExtrude","SWEPT_FACE",FACE,{"disambiguationData":[OSD([sQuery(id+"F6.wireOp",EDGE,"E27")])]}),makeQuery(id+"F8.opExtrude","SWEPT_FACE",FACE,{"disambiguationData":[OSD([subQ10])]}),makeQuery(id+"F8.opExtrude","SWEPT_FACE",FACE,{"disambiguationData":[OSD([subQ8])]}),makeQuery(id+"F8.opExtrude","SWEPT_FACE",FACE,{"disambiguationData":[OSD([subQ3,subQ1]),TDD([makeQuery(id+"F6.imprint","IMPRINT",EDGE,{"disambiguationData":[TD([[makeQuery(id+"F6.imprint","INTERSECT",VERTEX,{"derivedFrom":[subQ7,sQuery(id+"F6.wireOp",EDGE,"E41")]}),-1.0]])],"derivedFrom":subQ7})])]}),makeQuery(id+"F8.opExtrude","SWEPT_FACE",FACE,{"disambiguationData":[OSD([subQ3,subQ1]),TDD([makeQuery(id+"F6.imprint","IMPRINT",EDGE,{"disambiguationData":[TD([[makeQuery(id+"F6.imprint","INTERSECT",VERTEX,{"derivedFrom":[subQ7,sQuery(id+"F6.wireOp",EDGE,"E46")]}),1.0]])],"derivedFrom":subQ7})])]})])],"derivedFrom":makeQuery(id+"F2.boolean.opBoolean","MERGE",FACE,{"derivedFrom":[subQ5,subQ4]})})}),makeQuery(id+"F12.opExtrude","CAP_FACE",FACE,{"disambiguationData":[OSD([sQuery(id+"F11.wireOp",EDGE,"E50.3.3.0"),sQuery(id+"F11.wireOp",EDGE,"E50.1.4.0"),sQuery(id+"F11.wireOp",EDGE,"E58"),subQ0])],"isStart":true})]})]});}
            var Q3;
            {var subQ0=sQuery(id+"F11.wireOp",EDGE,"E73");var subQ1=sQuery(id+"F0.wireOp",EDGE,"E11");var subQ2=sQuery(id+"F0.wireOp",EDGE,"E10");var subQ3=makeQuery(id+"F2.opRevolve","SWEPT_FACE",FACE,{"disambiguationData":[OSD([subQ2])]});var subQ4=makeQuery(id+"F1.opExtrude","SWEPT_FACE",FACE,{"disambiguationData":[OSD([subQ2])]});var subQ5=sQuery(id+"F6.wireOp",EDGE,"E41");var subQ6=makeQuery(id+"F2.opRevolve","SWEPT_EDGE",EDGE,{"disambiguationData":[OSD([subQ2,subQ1])]});Q3=makeQuery(id+"F13.opChamfer","BLEND_EDGE",EDGE,{"blendedFrom":[makeQuery(id+"F12.opExtrude","CAP_EDGE",EDGE,{"disambiguationData":[OSD([subQ0])],"isStart":true}),makeQuery(id+"F12.boolean.opBoolean","MERGE",FACE,{"derivedFrom":[makeQuery(id+"F8.boolean.opBoolean","SPLIT",FACE,{"disambiguationData":[TD([subQ4,makeQuery(id+"F1.opExtrude","SWEPT_FACE",FACE,{"disambiguationData":[OSD([subQ1])]}),subQ3,makeQuery(id+"F2.opRevolve","SWEPT_FACE",FACE,{"disambiguationData":[OSD([subQ1])]}),makeQuery(id+"F8.opExtrude","SWEPT_FACE",FACE,{"disambiguationData":[OSD([subQ5])]}),makeQuery(id+"F8.opExtrude","SWEPT_FACE",FACE,{"disambiguationData":[OSD([sQuery(id+"F6.wireOp",EDGE,"E42")])]}),makeQuery(id+"F8.opExtrude","SWEPT_FACE",FACE,{"disambiguationData":[OSD([subQ2,subQ1]),TDD([makeQuery(id+"F6.imprint","IMPRINT",EDGE,{"disambiguationData":[TD([[makeQuery(id+"F6.imprint","INTERSECT",VERTEX,{"derivedFrom":[subQ6,subQ5]}),-1.0]])],"derivedFrom":subQ6})])]})])],"derivedFrom":makeQuery(id+"F2.boolean.opBoolean","MERGE",FACE,{"derivedFrom":[subQ4,subQ3]})}),makeQuery(id+"F12.opExtrude","CAP_FACE",FACE,{"disambiguationData":[OSD([sQuery(id+"F11.wireOp",EDGE,"E49.2.1"),sQuery(id+"F11.wireOp",EDGE,"E50.1.3.0"),sQuery(id+"F11.wireOp",EDGE,"E56"),subQ0])],"isStart":true})]})],"blendedInto":[makeQuery(id+"F12.boolean.opBoolean","MERGE",FACE,{"derivedFrom":[makeQuery(id+"F8.boolean.opBoolean","SPLIT",FACE,{"disambiguationData":[TD([subQ4,makeQuery(id+"F1.opExtrude","SWEPT_FACE",FACE,{"disambiguationData":[OSD([subQ1])]}),subQ3,makeQuery(id+"F2.opRevolve","SWEPT_FACE",FACE,{"disambiguationData":[OSD([subQ1])]}),makeQuery(id+"F8.opExtrude","SWEPT_FACE",FACE,{"disambiguationData":[OSD([subQ5])]}),makeQuery(id+"F8.opExtrude","SWEPT_FACE",FACE,{"disambiguationData":[OSD([sQuery(id+"F6.wireOp",EDGE,"E42")])]}),makeQuery(id+"F8.opExtrude","SWEPT_FACE",FACE,{"disambiguationData":[OSD([subQ2,subQ1]),TDD([makeQuery(id+"F6.imprint","IMPRINT",EDGE,{"disambiguationData":[TD([[makeQuery(id+"F6.imprint","INTERSECT",VERTEX,{"derivedFrom":[subQ6,subQ5]}),-1.0]])],"derivedFrom":subQ6})])]})])],"derivedFrom":makeQuery(id+"F2.boolean.opBoolean","MERGE",FACE,{"derivedFrom":[subQ4,subQ3]})}),makeQuery(id+"F12.opExtrude","CAP_FACE",FACE,{"disambiguationData":[OSD([sQuery(id+"F11.wireOp",EDGE,"E49.2.1"),sQuery(id+"F11.wireOp",EDGE,"E50.1.3.0"),sQuery(id+"F11.wireOp",EDGE,"E56"),subQ0])],"isStart":true})]})]});}
            var Q4;
            {var subQ0=sQuery(id+"F11.wireOp",EDGE,"E71");var subQ1=sQuery(id+"F0.wireOp",EDGE,"E11");var subQ2=sQuery(id+"F0.wireOp",EDGE,"E10");var subQ3=makeQuery(id+"F1.opExtrude","SWEPT_FACE",FACE,{"disambiguationData":[OSD([subQ2])]});var subQ4=makeQuery(id+"F2.opRevolve","SWEPT_FACE",FACE,{"disambiguationData":[OSD([subQ2])]});Q4=makeQuery(id+"F13.opChamfer","BLEND_EDGE",EDGE,{"blendedFrom":[makeQuery(id+"F12.opExtrude","CAP_EDGE",EDGE,{"disambiguationData":[OSD([subQ0])],"isStart":true}),makeQuery(id+"F12.boolean.opBoolean","MERGE",FACE,{"derivedFrom":[makeQuery(id+"F8.boolean.opBoolean","SPLIT",FACE,{"disambiguationData":[TD([subQ3,makeQuery(id+"F1.opExtrude","SWEPT_FACE",FACE,{"disambiguationData":[OSD([subQ1])]}),subQ4,makeQuery(id+"F2.opRevolve","SWEPT_FACE",FACE,{"disambiguationData":[OSD([subQ1])]}),makeQuery(id+"F7.opExtrude","SWEPT_FACE",FACE,{"disambiguationData":[OSD([sQuery(id+"F6.wireOp",EDGE,"E30")])]}),makeQuery(id+"F7.opExtrude","SWEPT_FACE",FACE,{"disambiguationData":[OSD([sQuery(id+"F6.wireOp",EDGE,"E31")])]}),makeQuery(id+"F8.opExtrude","SWEPT_FACE",FACE,{"disambiguationData":[OSD([sQuery(id+"F6.wireOp",EDGE,"E36")])]}),makeQuery(id+"F8.opExtrude","SWEPT_FACE",FACE,{"disambiguationData":[OSD([sQuery(id+"F6.wireOp",EDGE,"E37")])]}),makeQuery(id+"F8.opExtrude","SWEPT_FACE",FACE,{"disambiguationData":[OSD([sQuery(id+"F6.wireOp",EDGE,"E41")])]}),makeQuery(id+"F8.opExtrude","SWEPT_FACE",FACE,{"disambiguationData":[OSD([sQuery(id+"F6.wireOp",EDGE,"E42")])]}),makeQuery(id+"F8.opExtrude","SWEPT_FACE",FACE,{"disambiguationData":[OSD([sQuery(id+"F6.wireOp",EDGE,"E45")])]}),makeQuery(id+"F8.opExtrude","SWEPT_FACE",FACE,{"disambiguationData":[OSD([sQuery(id+"F6.wireOp",EDGE,"E46")])]})])],"derivedFrom":makeQuery(id+"F2.boolean.opBoolean","MERGE",FACE,{"derivedFrom":[subQ3,subQ4]})}),makeQuery(id+"F12.opExtrude","CAP_FACE",FACE,{"disambiguationData":[OSD([sQuery(id+"F11.wireOp",EDGE,"E47"),sQuery(id+"F11.wireOp",EDGE,"E50.3.7.0"),sQuery(id+"F11.wireOp",EDGE,"E66"),sQuery(id+"F11.wireOp",EDGE,"E67")])],"isStart":true}),makeQuery(id+"F12.opExtrude","CAP_FACE",FACE,{"disambiguationData":[OSD([sQuery(id+"F11.wireOp",EDGE,"E48"),sQuery(id+"F11.wireOp",EDGE,"E49.1.0"),sQuery(id+"F11.wireOp",EDGE,"E52"),sQuery(id+"F11.wireOp",EDGE,"E69")])],"isStart":true}),makeQuery(id+"F12.opExtrude","CAP_FACE",FACE,{"disambiguationData":[OSD([sQuery(id+"F11.wireOp",EDGE,"E49.1.1"),sQuery(id+"F11.wireOp",EDGE,"E49.2.0"),sQuery(id+"F11.wireOp",EDGE,"E54"),subQ0])],"isStart":true}),makeQuery(id+"F12.opExtrude","CAP_FACE",FACE,{"disambiguationData":[OSD([sQuery(id+"F11.wireOp",EDGE,"E50.3.6.0"),sQuery(id+"F11.wireOp",EDGE,"E50.1.7.0"),sQuery(id+"F11.wireOp",EDGE,"E64"),sQuery(id+"F11.wireOp",EDGE,"E81")])],"isStart":true})]})],"blendedInto":[makeQuery(id+"F12.boolean.opBoolean","MERGE",FACE,{"derivedFrom":[makeQuery(id+"F8.boolean.opBoolean","SPLIT",FACE,{"disambiguationData":[TD([subQ3,makeQuery(id+"F1.opExtrude","SWEPT_FACE",FACE,{"disambiguationData":[OSD([subQ1])]}),subQ4,makeQuery(id+"F2.opRevolve","SWEPT_FACE",FACE,{"disambiguationData":[OSD([subQ1])]}),makeQuery(id+"F7.opExtrude","SWEPT_FACE",FACE,{"disambiguationData":[OSD([sQuery(id+"F6.wireOp",EDGE,"E30")])]}),makeQuery(id+"F7.opExtrude","SWEPT_FACE",FACE,{"disambiguationData":[OSD([sQuery(id+"F6.wireOp",EDGE,"E31")])]}),makeQuery(id+"F8.opExtrude","SWEPT_FACE",FACE,{"disambiguationData":[OSD([sQuery(id+"F6.wireOp",EDGE,"E36")])]}),makeQuery(id+"F8.opExtrude","SWEPT_FACE",FACE,{"disambiguationData":[OSD([sQuery(id+"F6.wireOp",EDGE,"E37")])]}),makeQuery(id+"F8.opExtrude","SWEPT_FACE",FACE,{"disambiguationData":[OSD([sQuery(id+"F6.wireOp",EDGE,"E41")])]}),makeQuery(id+"F8.opExtrude","SWEPT_FACE",FACE,{"disambiguationData":[OSD([sQuery(id+"F6.wireOp",EDGE,"E42")])]}),makeQuery(id+"F8.opExtrude","SWEPT_FACE",FACE,{"disambiguationData":[OSD([sQuery(id+"F6.wireOp",EDGE,"E45")])]}),makeQuery(id+"F8.opExtrude","SWEPT_FACE",FACE,{"disambiguationData":[OSD([sQuery(id+"F6.wireOp",EDGE,"E46")])]})])],"derivedFrom":makeQuery(id+"F2.boolean.opBoolean","MERGE",FACE,{"derivedFrom":[subQ3,subQ4]})}),makeQuery(id+"F12.opExtrude","CAP_FACE",FACE,{"disambiguationData":[OSD([sQuery(id+"F11.wireOp",EDGE,"E47"),sQuery(id+"F11.wireOp",EDGE,"E50.3.7.0"),sQuery(id+"F11.wireOp",EDGE,"E66"),sQuery(id+"F11.wireOp",EDGE,"E67")])],"isStart":true}),makeQuery(id+"F12.opExtrude","CAP_FACE",FACE,{"disambiguationData":[OSD([sQuery(id+"F11.wireOp",EDGE,"E48"),sQuery(id+"F11.wireOp",EDGE,"E49.1.0"),sQuery(id+"F11.wireOp",EDGE,"E52"),sQuery(id+"F11.wireOp",EDGE,"E69")])],"isStart":true}),makeQuery(id+"F12.opExtrude","CAP_FACE",FACE,{"disambiguationData":[OSD([sQuery(id+"F11.wireOp",EDGE,"E49.1.1"),sQuery(id+"F11.wireOp",EDGE,"E49.2.0"),sQuery(id+"F11.wireOp",EDGE,"E54"),subQ0])],"isStart":true}),makeQuery(id+"F12.opExtrude","CAP_FACE",FACE,{"disambiguationData":[OSD([sQuery(id+"F11.wireOp",EDGE,"E50.3.6.0"),sQuery(id+"F11.wireOp",EDGE,"E50.1.7.0"),sQuery(id+"F11.wireOp",EDGE,"E64"),sQuery(id+"F11.wireOp",EDGE,"E81")])],"isStart":true})]})]});}
            var Q5;
            {var subQ0=sQuery(id+"F11.wireOp",EDGE,"E69");var subQ1=sQuery(id+"F0.wireOp",EDGE,"E11");var subQ2=sQuery(id+"F0.wireOp",EDGE,"E10");var subQ3=makeQuery(id+"F1.opExtrude","SWEPT_FACE",FACE,{"disambiguationData":[OSD([subQ2])]});var subQ4=makeQuery(id+"F2.opRevolve","SWEPT_FACE",FACE,{"disambiguationData":[OSD([subQ2])]});Q5=makeQuery(id+"F13.opChamfer","BLEND_EDGE",EDGE,{"blendedFrom":[makeQuery(id+"F12.opExtrude","CAP_EDGE",EDGE,{"disambiguationData":[OSD([subQ0])],"isStart":true}),makeQuery(id+"F12.boolean.opBoolean","MERGE",FACE,{"derivedFrom":[makeQuery(id+"F8.boolean.opBoolean","SPLIT",FACE,{"disambiguationData":[TD([subQ3,makeQuery(id+"F1.opExtrude","SWEPT_FACE",FACE,{"disambiguationData":[OSD([subQ1])]}),subQ4,makeQuery(id+"F2.opRevolve","SWEPT_FACE",FACE,{"disambiguationData":[OSD([subQ1])]}),makeQuery(id+"F7.opExtrude","SWEPT_FACE",FACE,{"disambiguationData":[OSD([sQuery(id+"F6.wireOp",EDGE,"E30")])]}),makeQuery(id+"F7.opExtrude","SWEPT_FACE",FACE,{"disambiguationData":[OSD([sQuery(id+"F6.wireOp",EDGE,"E31")])]}),makeQuery(id+"F8.opExtrude","SWEPT_FACE",FACE,{"disambiguationData":[OSD([sQuery(id+"F6.wireOp",EDGE,"E36")])]}),makeQuery(id+"F8.opExtrude","SWEPT_FACE",FACE,{"disambiguationData":[OSD([sQuery(id+"F6.wireOp",EDGE,"E37")])]}),makeQuery(id+"F8.opExtrude","SWEPT_FACE",FACE,{"disambiguationData":[OSD([sQuery(id+"F6.wireOp",EDGE,"E41")])]}),makeQuery(id+"F8.opExtrude","SWEPT_FACE",FACE,{"disambiguationData":[OSD([sQuery(id+"F6.wireOp",EDGE,"E42")])]}),makeQuery(id+"F8.opExtrude","SWEPT_FACE",FACE,{"disambiguationData":[OSD([sQuery(id+"F6.wireOp",EDGE,"E45")])]}),makeQuery(id+"F8.opExtrude","SWEPT_FACE",FACE,{"disambiguationData":[OSD([sQuery(id+"F6.wireOp",EDGE,"E46")])]})])],"derivedFrom":makeQuery(id+"F2.boolean.opBoolean","MERGE",FACE,{"derivedFrom":[subQ3,subQ4]})}),makeQuery(id+"F12.opExtrude","CAP_FACE",FACE,{"disambiguationData":[OSD([sQuery(id+"F11.wireOp",EDGE,"E47"),sQuery(id+"F11.wireOp",EDGE,"E50.3.7.0"),sQuery(id+"F11.wireOp",EDGE,"E66"),sQuery(id+"F11.wireOp",EDGE,"E67")])],"isStart":true}),makeQuery(id+"F12.opExtrude","CAP_FACE",FACE,{"disambiguationData":[OSD([sQuery(id+"F11.wireOp",EDGE,"E48"),sQuery(id+"F11.wireOp",EDGE,"E49.1.0"),sQuery(id+"F11.wireOp",EDGE,"E52"),subQ0])],"isStart":true}),makeQuery(id+"F12.opExtrude","CAP_FACE",FACE,{"disambiguationData":[OSD([sQuery(id+"F11.wireOp",EDGE,"E49.1.1"),sQuery(id+"F11.wireOp",EDGE,"E49.2.0"),sQuery(id+"F11.wireOp",EDGE,"E54"),sQuery(id+"F11.wireOp",EDGE,"E71")])],"isStart":true}),makeQuery(id+"F12.opExtrude","CAP_FACE",FACE,{"disambiguationData":[OSD([sQuery(id+"F11.wireOp",EDGE,"E50.3.6.0"),sQuery(id+"F11.wireOp",EDGE,"E50.1.7.0"),sQuery(id+"F11.wireOp",EDGE,"E64"),sQuery(id+"F11.wireOp",EDGE,"E81")])],"isStart":true})]})],"blendedInto":[makeQuery(id+"F12.boolean.opBoolean","MERGE",FACE,{"derivedFrom":[makeQuery(id+"F8.boolean.opBoolean","SPLIT",FACE,{"disambiguationData":[TD([subQ3,makeQuery(id+"F1.opExtrude","SWEPT_FACE",FACE,{"disambiguationData":[OSD([subQ1])]}),subQ4,makeQuery(id+"F2.opRevolve","SWEPT_FACE",FACE,{"disambiguationData":[OSD([subQ1])]}),makeQuery(id+"F7.opExtrude","SWEPT_FACE",FACE,{"disambiguationData":[OSD([sQuery(id+"F6.wireOp",EDGE,"E30")])]}),makeQuery(id+"F7.opExtrude","SWEPT_FACE",FACE,{"disambiguationData":[OSD([sQuery(id+"F6.wireOp",EDGE,"E31")])]}),makeQuery(id+"F8.opExtrude","SWEPT_FACE",FACE,{"disambiguationData":[OSD([sQuery(id+"F6.wireOp",EDGE,"E36")])]}),makeQuery(id+"F8.opExtrude","SWEPT_FACE",FACE,{"disambiguationData":[OSD([sQuery(id+"F6.wireOp",EDGE,"E37")])]}),makeQuery(id+"F8.opExtrude","SWEPT_FACE",FACE,{"disambiguationData":[OSD([sQuery(id+"F6.wireOp",EDGE,"E41")])]}),makeQuery(id+"F8.opExtrude","SWEPT_FACE",FACE,{"disambiguationData":[OSD([sQuery(id+"F6.wireOp",EDGE,"E42")])]}),makeQuery(id+"F8.opExtrude","SWEPT_FACE",FACE,{"disambiguationData":[OSD([sQuery(id+"F6.wireOp",EDGE,"E45")])]}),makeQuery(id+"F8.opExtrude","SWEPT_FACE",FACE,{"disambiguationData":[OSD([sQuery(id+"F6.wireOp",EDGE,"E46")])]})])],"derivedFrom":makeQuery(id+"F2.boolean.opBoolean","MERGE",FACE,{"derivedFrom":[subQ3,subQ4]})}),makeQuery(id+"F12.opExtrude","CAP_FACE",FACE,{"disambiguationData":[OSD([sQuery(id+"F11.wireOp",EDGE,"E47"),sQuery(id+"F11.wireOp",EDGE,"E50.3.7.0"),sQuery(id+"F11.wireOp",EDGE,"E66"),sQuery(id+"F11.wireOp",EDGE,"E67")])],"isStart":true}),makeQuery(id+"F12.opExtrude","CAP_FACE",FACE,{"disambiguationData":[OSD([sQuery(id+"F11.wireOp",EDGE,"E48"),sQuery(id+"F11.wireOp",EDGE,"E49.1.0"),sQuery(id+"F11.wireOp",EDGE,"E52"),subQ0])],"isStart":true}),makeQuery(id+"F12.opExtrude","CAP_FACE",FACE,{"disambiguationData":[OSD([sQuery(id+"F11.wireOp",EDGE,"E49.1.1"),sQuery(id+"F11.wireOp",EDGE,"E49.2.0"),sQuery(id+"F11.wireOp",EDGE,"E54"),sQuery(id+"F11.wireOp",EDGE,"E71")])],"isStart":true}),makeQuery(id+"F12.opExtrude","CAP_FACE",FACE,{"disambiguationData":[OSD([sQuery(id+"F11.wireOp",EDGE,"E50.3.6.0"),sQuery(id+"F11.wireOp",EDGE,"E50.1.7.0"),sQuery(id+"F11.wireOp",EDGE,"E64"),sQuery(id+"F11.wireOp",EDGE,"E81")])],"isStart":true})]})]});}
            var Q6;
            {var subQ0=sQuery(id+"F11.wireOp",EDGE,"E67");var subQ1=sQuery(id+"F0.wireOp",EDGE,"E11");var subQ2=sQuery(id+"F0.wireOp",EDGE,"E10");var subQ3=makeQuery(id+"F1.opExtrude","SWEPT_FACE",FACE,{"disambiguationData":[OSD([subQ2])]});var subQ4=makeQuery(id+"F2.opRevolve","SWEPT_FACE",FACE,{"disambiguationData":[OSD([subQ2])]});Q6=makeQuery(id+"F13.opChamfer","BLEND_EDGE",EDGE,{"blendedFrom":[makeQuery(id+"F12.opExtrude","CAP_EDGE",EDGE,{"disambiguationData":[OSD([subQ0])],"isStart":true}),makeQuery(id+"F12.boolean.opBoolean","MERGE",FACE,{"derivedFrom":[makeQuery(id+"F8.boolean.opBoolean","SPLIT",FACE,{"disambiguationData":[TD([subQ3,makeQuery(id+"F1.opExtrude","SWEPT_FACE",FACE,{"disambiguationData":[OSD([subQ1])]}),subQ4,makeQuery(id+"F2.opRevolve","SWEPT_FACE",FACE,{"disambiguationData":[OSD([subQ1])]}),makeQuery(id+"F7.opExtrude","SWEPT_FACE",FACE,{"disambiguationData":[OSD([sQuery(id+"F6.wireOp",EDGE,"E30")])]}),makeQuery(id+"F7.opExtrude","SWEPT_FACE",FACE,{"disambiguationData":[OSD([sQuery(id+"F6.wireOp",EDGE,"E31")])]}),makeQuery(id+"F8.opExtrude","SWEPT_FACE",FACE,{"disambiguationData":[OSD([sQuery(id+"F6.wireOp",EDGE,"E36")])]}),makeQuery(id+"F8.opExtrude","SWEPT_FACE",FACE,{"disambiguationData":[OSD([sQuery(id+"F6.wireOp",EDGE,"E37")])]}),makeQuery(id+"F8.opExtrude","SWEPT_FACE",FACE,{"disambiguationData":[OSD([sQuery(id+"F6.wireOp",EDGE,"E41")])]}),makeQuery(id+"F8.opExtrude","SWEPT_FACE",FACE,{"disambiguationData":[OSD([sQuery(id+"F6.wireOp",EDGE,"E42")])]}),makeQuery(id+"F8.opExtrude","SWEPT_FACE",FACE,{"disambiguationData":[OSD([sQuery(id+"F6.wireOp",EDGE,"E45")])]}),makeQuery(id+"F8.opExtrude","SWEPT_FACE",FACE,{"disambiguationData":[OSD([sQuery(id+"F6.wireOp",EDGE,"E46")])]})])],"derivedFrom":makeQuery(id+"F2.boolean.opBoolean","MERGE",FACE,{"derivedFrom":[subQ3,subQ4]})}),makeQuery(id+"F12.opExtrude","CAP_FACE",FACE,{"disambiguationData":[OSD([sQuery(id+"F11.wireOp",EDGE,"E47"),sQuery(id+"F11.wireOp",EDGE,"E50.3.7.0"),sQuery(id+"F11.wireOp",EDGE,"E66"),subQ0])],"isStart":true}),makeQuery(id+"F12.opExtrude","CAP_FACE",FACE,{"disambiguationData":[OSD([sQuery(id+"F11.wireOp",EDGE,"E48"),sQuery(id+"F11.wireOp",EDGE,"E49.1.0"),sQuery(id+"F11.wireOp",EDGE,"E52"),sQuery(id+"F11.wireOp",EDGE,"E69")])],"isStart":true}),makeQuery(id+"F12.opExtrude","CAP_FACE",FACE,{"disambiguationData":[OSD([sQuery(id+"F11.wireOp",EDGE,"E49.1.1"),sQuery(id+"F11.wireOp",EDGE,"E49.2.0"),sQuery(id+"F11.wireOp",EDGE,"E54"),sQuery(id+"F11.wireOp",EDGE,"E71")])],"isStart":true}),makeQuery(id+"F12.opExtrude","CAP_FACE",FACE,{"disambiguationData":[OSD([sQuery(id+"F11.wireOp",EDGE,"E50.3.6.0"),sQuery(id+"F11.wireOp",EDGE,"E50.1.7.0"),sQuery(id+"F11.wireOp",EDGE,"E64"),sQuery(id+"F11.wireOp",EDGE,"E81")])],"isStart":true})]})],"blendedInto":[makeQuery(id+"F12.boolean.opBoolean","MERGE",FACE,{"derivedFrom":[makeQuery(id+"F8.boolean.opBoolean","SPLIT",FACE,{"disambiguationData":[TD([subQ3,makeQuery(id+"F1.opExtrude","SWEPT_FACE",FACE,{"disambiguationData":[OSD([subQ1])]}),subQ4,makeQuery(id+"F2.opRevolve","SWEPT_FACE",FACE,{"disambiguationData":[OSD([subQ1])]}),makeQuery(id+"F7.opExtrude","SWEPT_FACE",FACE,{"disambiguationData":[OSD([sQuery(id+"F6.wireOp",EDGE,"E30")])]}),makeQuery(id+"F7.opExtrude","SWEPT_FACE",FACE,{"disambiguationData":[OSD([sQuery(id+"F6.wireOp",EDGE,"E31")])]}),makeQuery(id+"F8.opExtrude","SWEPT_FACE",FACE,{"disambiguationData":[OSD([sQuery(id+"F6.wireOp",EDGE,"E36")])]}),makeQuery(id+"F8.opExtrude","SWEPT_FACE",FACE,{"disambiguationData":[OSD([sQuery(id+"F6.wireOp",EDGE,"E37")])]}),makeQuery(id+"F8.opExtrude","SWEPT_FACE",FACE,{"disambiguationData":[OSD([sQuery(id+"F6.wireOp",EDGE,"E41")])]}),makeQuery(id+"F8.opExtrude","SWEPT_FACE",FACE,{"disambiguationData":[OSD([sQuery(id+"F6.wireOp",EDGE,"E42")])]}),makeQuery(id+"F8.opExtrude","SWEPT_FACE",FACE,{"disambiguationData":[OSD([sQuery(id+"F6.wireOp",EDGE,"E45")])]}),makeQuery(id+"F8.opExtrude","SWEPT_FACE",FACE,{"disambiguationData":[OSD([sQuery(id+"F6.wireOp",EDGE,"E46")])]})])],"derivedFrom":makeQuery(id+"F2.boolean.opBoolean","MERGE",FACE,{"derivedFrom":[subQ3,subQ4]})}),makeQuery(id+"F12.opExtrude","CAP_FACE",FACE,{"disambiguationData":[OSD([sQuery(id+"F11.wireOp",EDGE,"E47"),sQuery(id+"F11.wireOp",EDGE,"E50.3.7.0"),sQuery(id+"F11.wireOp",EDGE,"E66"),subQ0])],"isStart":true}),makeQuery(id+"F12.opExtrude","CAP_FACE",FACE,{"disambiguationData":[OSD([sQuery(id+"F11.wireOp",EDGE,"E48"),sQuery(id+"F11.wireOp",EDGE,"E49.1.0"),sQuery(id+"F11.wireOp",EDGE,"E52"),sQuery(id+"F11.wireOp",EDGE,"E69")])],"isStart":true}),makeQuery(id+"F12.opExtrude","CAP_FACE",FACE,{"disambiguationData":[OSD([sQuery(id+"F11.wireOp",EDGE,"E49.1.1"),sQuery(id+"F11.wireOp",EDGE,"E49.2.0"),sQuery(id+"F11.wireOp",EDGE,"E54"),sQuery(id+"F11.wireOp",EDGE,"E71")])],"isStart":true}),makeQuery(id+"F12.opExtrude","CAP_FACE",FACE,{"disambiguationData":[OSD([sQuery(id+"F11.wireOp",EDGE,"E50.3.6.0"),sQuery(id+"F11.wireOp",EDGE,"E50.1.7.0"),sQuery(id+"F11.wireOp",EDGE,"E64"),sQuery(id+"F11.wireOp",EDGE,"E81")])],"isStart":true})]})]});}
            var Q7;
            {var subQ0=sQuery(id+"F11.wireOp",EDGE,"E81");var subQ1=sQuery(id+"F0.wireOp",EDGE,"E11");var subQ2=sQuery(id+"F0.wireOp",EDGE,"E10");var subQ3=makeQuery(id+"F1.opExtrude","SWEPT_FACE",FACE,{"disambiguationData":[OSD([subQ2])]});var subQ4=makeQuery(id+"F2.opRevolve","SWEPT_FACE",FACE,{"disambiguationData":[OSD([subQ2])]});Q7=makeQuery(id+"F13.opChamfer","BLEND_EDGE",EDGE,{"blendedFrom":[makeQuery(id+"F12.opExtrude","CAP_EDGE",EDGE,{"disambiguationData":[OSD([subQ0])],"isStart":true}),makeQuery(id+"F12.boolean.opBoolean","MERGE",FACE,{"derivedFrom":[makeQuery(id+"F8.boolean.opBoolean","SPLIT",FACE,{"disambiguationData":[TD([subQ3,makeQuery(id+"F1.opExtrude","SWEPT_FACE",FACE,{"disambiguationData":[OSD([subQ1])]}),subQ4,makeQuery(id+"F2.opRevolve","SWEPT_FACE",FACE,{"disambiguationData":[OSD([subQ1])]}),makeQuery(id+"F7.opExtrude","SWEPT_FACE",FACE,{"disambiguationData":[OSD([sQuery(id+"F6.wireOp",EDGE,"E30")])]}),makeQuery(id+"F7.opExtrude","SWEPT_FACE",FACE,{"disambiguationData":[OSD([sQuery(id+"F6.wireOp",EDGE,"E31")])]}),makeQuery(id+"F8.opExtrude","SWEPT_FACE",FACE,{"disambiguationData":[OSD([sQuery(id+"F6.wireOp",EDGE,"E36")])]}),makeQuery(id+"F8.opExtrude","SWEPT_FACE",FACE,{"disambiguationData":[OSD([sQuery(id+"F6.wireOp",EDGE,"E37")])]}),makeQuery(id+"F8.opExtrude","SWEPT_FACE",FACE,{"disambiguationData":[OSD([sQuery(id+"F6.wireOp",EDGE,"E41")])]}),makeQuery(id+"F8.opExtrude","SWEPT_FACE",FACE,{"disambiguationData":[OSD([sQuery(id+"F6.wireOp",EDGE,"E42")])]}),makeQuery(id+"F8.opExtrude","SWEPT_FACE",FACE,{"disambiguationData":[OSD([sQuery(id+"F6.wireOp",EDGE,"E45")])]}),makeQuery(id+"F8.opExtrude","SWEPT_FACE",FACE,{"disambiguationData":[OSD([sQuery(id+"F6.wireOp",EDGE,"E46")])]})])],"derivedFrom":makeQuery(id+"F2.boolean.opBoolean","MERGE",FACE,{"derivedFrom":[subQ3,subQ4]})}),makeQuery(id+"F12.opExtrude","CAP_FACE",FACE,{"disambiguationData":[OSD([sQuery(id+"F11.wireOp",EDGE,"E47"),sQuery(id+"F11.wireOp",EDGE,"E50.3.7.0"),sQuery(id+"F11.wireOp",EDGE,"E66"),sQuery(id+"F11.wireOp",EDGE,"E67")])],"isStart":true}),makeQuery(id+"F12.opExtrude","CAP_FACE",FACE,{"disambiguationData":[OSD([sQuery(id+"F11.wireOp",EDGE,"E48"),sQuery(id+"F11.wireOp",EDGE,"E49.1.0"),sQuery(id+"F11.wireOp",EDGE,"E52"),sQuery(id+"F11.wireOp",EDGE,"E69")])],"isStart":true}),makeQuery(id+"F12.opExtrude","CAP_FACE",FACE,{"disambiguationData":[OSD([sQuery(id+"F11.wireOp",EDGE,"E49.1.1"),sQuery(id+"F11.wireOp",EDGE,"E49.2.0"),sQuery(id+"F11.wireOp",EDGE,"E54"),sQuery(id+"F11.wireOp",EDGE,"E71")])],"isStart":true}),makeQuery(id+"F12.opExtrude","CAP_FACE",FACE,{"disambiguationData":[OSD([sQuery(id+"F11.wireOp",EDGE,"E50.3.6.0"),sQuery(id+"F11.wireOp",EDGE,"E50.1.7.0"),sQuery(id+"F11.wireOp",EDGE,"E64"),subQ0])],"isStart":true})]})],"blendedInto":[makeQuery(id+"F12.boolean.opBoolean","MERGE",FACE,{"derivedFrom":[makeQuery(id+"F8.boolean.opBoolean","SPLIT",FACE,{"disambiguationData":[TD([subQ3,makeQuery(id+"F1.opExtrude","SWEPT_FACE",FACE,{"disambiguationData":[OSD([subQ1])]}),subQ4,makeQuery(id+"F2.opRevolve","SWEPT_FACE",FACE,{"disambiguationData":[OSD([subQ1])]}),makeQuery(id+"F7.opExtrude","SWEPT_FACE",FACE,{"disambiguationData":[OSD([sQuery(id+"F6.wireOp",EDGE,"E30")])]}),makeQuery(id+"F7.opExtrude","SWEPT_FACE",FACE,{"disambiguationData":[OSD([sQuery(id+"F6.wireOp",EDGE,"E31")])]}),makeQuery(id+"F8.opExtrude","SWEPT_FACE",FACE,{"disambiguationData":[OSD([sQuery(id+"F6.wireOp",EDGE,"E36")])]}),makeQuery(id+"F8.opExtrude","SWEPT_FACE",FACE,{"disambiguationData":[OSD([sQuery(id+"F6.wireOp",EDGE,"E37")])]}),makeQuery(id+"F8.opExtrude","SWEPT_FACE",FACE,{"disambiguationData":[OSD([sQuery(id+"F6.wireOp",EDGE,"E41")])]}),makeQuery(id+"F8.opExtrude","SWEPT_FACE",FACE,{"disambiguationData":[OSD([sQuery(id+"F6.wireOp",EDGE,"E42")])]}),makeQuery(id+"F8.opExtrude","SWEPT_FACE",FACE,{"disambiguationData":[OSD([sQuery(id+"F6.wireOp",EDGE,"E45")])]}),makeQuery(id+"F8.opExtrude","SWEPT_FACE",FACE,{"disambiguationData":[OSD([sQuery(id+"F6.wireOp",EDGE,"E46")])]})])],"derivedFrom":makeQuery(id+"F2.boolean.opBoolean","MERGE",FACE,{"derivedFrom":[subQ3,subQ4]})}),makeQuery(id+"F12.opExtrude","CAP_FACE",FACE,{"disambiguationData":[OSD([sQuery(id+"F11.wireOp",EDGE,"E47"),sQuery(id+"F11.wireOp",EDGE,"E50.3.7.0"),sQuery(id+"F11.wireOp",EDGE,"E66"),sQuery(id+"F11.wireOp",EDGE,"E67")])],"isStart":true}),makeQuery(id+"F12.opExtrude","CAP_FACE",FACE,{"disambiguationData":[OSD([sQuery(id+"F11.wireOp",EDGE,"E48"),sQuery(id+"F11.wireOp",EDGE,"E49.1.0"),sQuery(id+"F11.wireOp",EDGE,"E52"),sQuery(id+"F11.wireOp",EDGE,"E69")])],"isStart":true}),makeQuery(id+"F12.opExtrude","CAP_FACE",FACE,{"disambiguationData":[OSD([sQuery(id+"F11.wireOp",EDGE,"E49.1.1"),sQuery(id+"F11.wireOp",EDGE,"E49.2.0"),sQuery(id+"F11.wireOp",EDGE,"E54"),sQuery(id+"F11.wireOp",EDGE,"E71")])],"isStart":true}),makeQuery(id+"F12.opExtrude","CAP_FACE",FACE,{"disambiguationData":[OSD([sQuery(id+"F11.wireOp",EDGE,"E50.3.6.0"),sQuery(id+"F11.wireOp",EDGE,"E50.1.7.0"),sQuery(id+"F11.wireOp",EDGE,"E64"),subQ0])],"isStart":true})]})]});}
            fillet(context, id + "F17", {"entities" : qUnion([Q0, Q1, Q2, Q3, Q4, Q5, Q6, Q7]), "radius" : 0.5 * mm, "tangentPropagation" : true, "allowEdgeOverflow" : false});
        }
        {
            var Q0;
            Q0 = qSketchRegion(id + "F11", true);
            extrude(context, id + "F18", {"entities" : qUnion([Q0]), "operationType" : NewBodyOperationType.ADD, "depth" : 2.45 * mm});
        }
        {
            var Q0;
            Q0=makeQuery(id+"F8.opExtrude","CAP_EDGE",EDGE,{"disambiguationData":[OSD([sQuery(id+"F6.wireOp",EDGE,"E42")])],"isStart":false});
            cPoint(context, id + "F19", {"entities" : qUnion([Q0]), "parameter" : 0.5});
        }
        {
            var Q0;
            Q0=makeQuery(id+"F1.opExtrude","CAP_VERTEX",VERTEX,{"disambiguationData":[OSD([sQuery(id+"F0.wireOp",EDGE,"E8"),sQuery(id+"F0.wireOp",EDGE,"E11")])],"isStart":false});
            var Q1;
            Q1 = qCreatedBy(id + "F19" ,VERTEX);
            var Q2;
            Q2=makeQuery(id+"F8.opExtrude","CAP_VERTEX",VERTEX,{"disambiguationData":[OSD([sQuery(id+"F0.wireOp",EDGE,"E10"),sQuery(id+"F0.wireOp",EDGE,"E11"),sQuery(id+"F6.wireOp",EDGE,"E41"),sQuery(id+"F6.wireOp",EDGE,"E42")])],"isStart":false});
            cPlane(context, id + "F20", {"entities" : qUnion([Q0, Q1, Q2]), "cplaneType" : CPlaneType.THREE_POINT, "offset" : 25 * mm, "width" : 150 * mm, "height" : 150 * mm});
        }
    });
